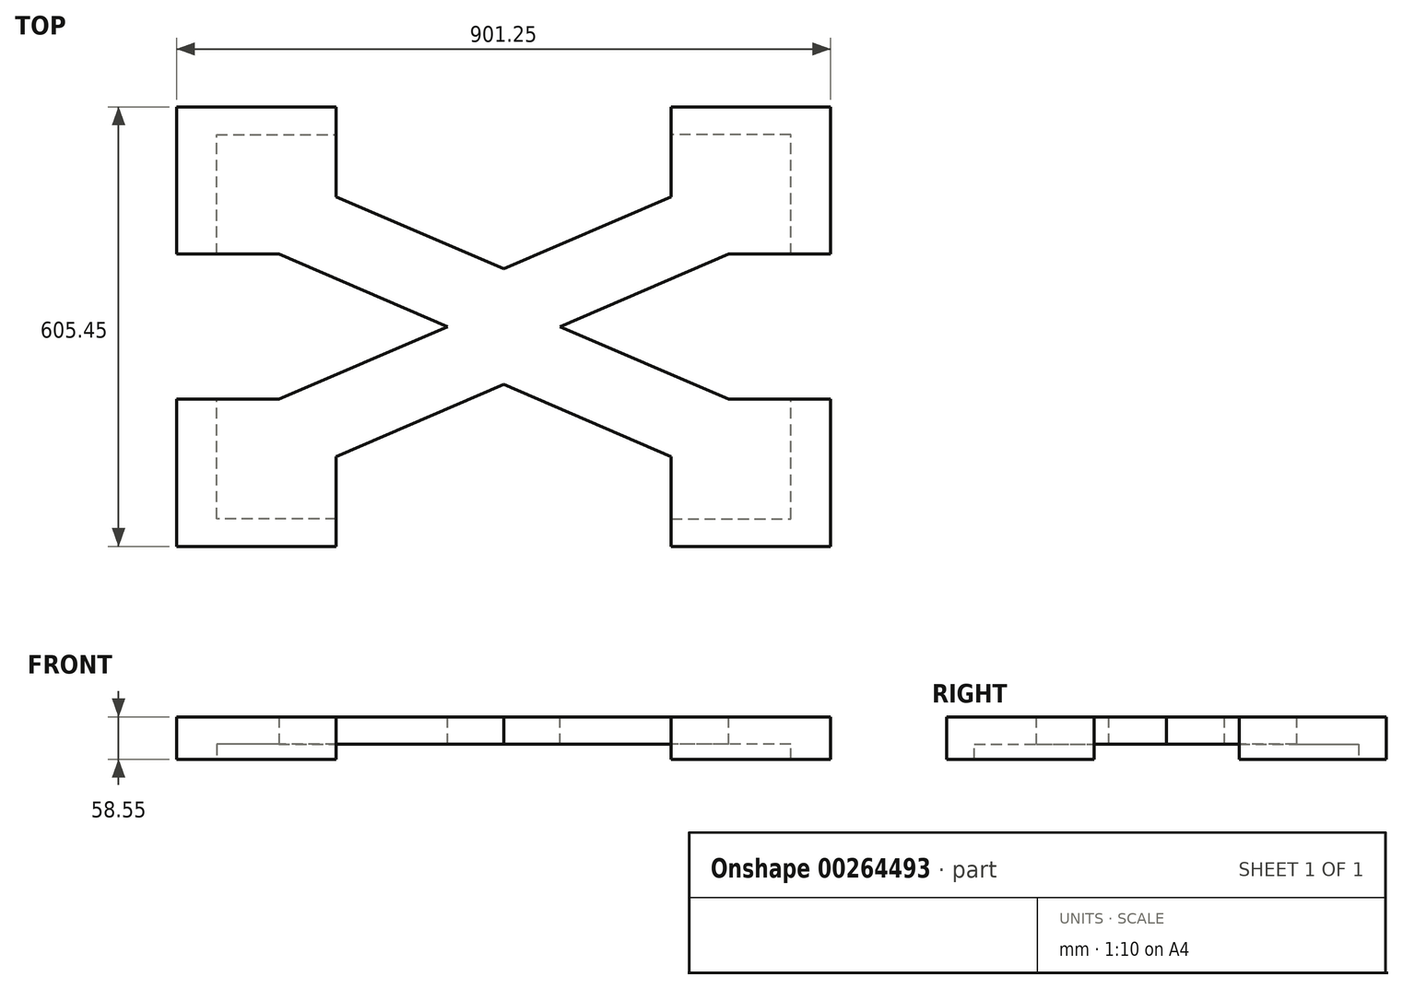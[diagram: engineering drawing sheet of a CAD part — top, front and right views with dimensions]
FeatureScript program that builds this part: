
annotation { "Feature Type Name" : "Feature", "Feature Type Description" : "" }
export const myFeature = defineFeature(function(context is Context, id is Id, definition is map)
    precondition{}
    {
        {
            var Q0;
            Q0=qCreatedBy(makeId("Top.planeOp"),FACE);
            var sketch = newSketch(context, id + "F0", { "sketchPlane" : qUnion([Q0])});
            skLineSegment(sketch, "E0", {"start": v(107.86, 53.86) * mm, "end": v(107.86, 107.86) * mm});
            skLineSegment(sketch, "E1", {"start": v(107.86, 107.86) * mm, "end": v(-107.86, 107.86) * mm});
            skLineSegment(sketch, "E2", {"start": v(-107.86, 107.86) * mm, "end": v(-107.86, -107.86) * mm});
            skLineSegment(sketch, "E3", {"start": v(-107.86, -107.86) * mm, "end": v(-53.86, -107.86) * mm});
            skLineSegment(sketch, "E4", {"start": v(-53.86, -107.86) * mm, "end": v(-53.86, 53.86) * mm});
            skLineSegment(sketch, "E5", {"start": v(-53.86, 53.86) * mm, "end": v(107.86, 53.86) * mm});
            skLineSegment(sketch, "E6", {"start": v(0, 107.86) * mm, "end": v(0, 0) * mm, "construction": true});
            skLineSegment(sketch, "E7", {"start": v(0, 0) * mm, "end": v(-107.86, 0) * mm, "construction": true});
            skSolve(sketch);
        }
        {
            var Q0;
            Q0=makeQuery(id+"F0.imprint","IMPRINT",FACE,{"disambiguationData":[TD([[makeQuery(id+"F0.imprint","IMPRINT",EDGE,{"derivedFrom":sQuery(id+"F0.wireOp",EDGE,"E0")}),1.0]])]});
            extrude(context, id + "F1", {"entities" : qUnion([Q0]), "depth" : 20.55 * mm});
        }
        {
            var Q0;
            Q0=makeQuery(id+"F1.opExtrude","CAP_FACE",FACE,{"disambiguationData":[OSD([sQuery(id+"F0.wireOp",EDGE,"E0"),sQuery(id+"F0.wireOp",EDGE,"E1"),sQuery(id+"F0.wireOp",EDGE,"E2"),sQuery(id+"F0.wireOp",EDGE,"E3"),sQuery(id+"F0.wireOp",EDGE,"E4"),sQuery(id+"F0.wireOp",EDGE,"E5")])],"isStart":false});
            var sketch = newSketch(context, id + "F2", { "sketchPlane" : qUnion([Q0])});
            skLineSegment(sketch, "E8.bottom", {"start": v(-107.86, 107.86) * mm, "end": v(107.86, 107.86) * mm});
            skLineSegment(sketch, "E8.top", {"start": v(-107.86, -107.86) * mm, "end": v(107.86, -107.86) * mm});
            skLineSegment(sketch, "E8.left", {"start": v(-107.86, 107.86) * mm, "end": v(-107.86, -107.86) * mm});
            skLineSegment(sketch, "E8.right", {"start": v(107.86, 107.86) * mm, "end": v(107.86, -107.86) * mm});
            skSolve(sketch);
        }
        {
            var Q0;
            Q0=qSketchRegion(id+"F2",true);
            extrude(context, id + "F3", {"entities" : qUnion([Q0]), "operationType" : NewBodyOperationType.ADD, "depth" : 38 * mm});
        }
        {
            var Q0;
            Q0=makeQuery(id+"F3.opExtrude","CAP_FACE",FACE,{"disambiguationData":[OSD([sQuery(id+"F2.wireOp",EDGE,"E8.bottom"),sQuery(id+"F2.wireOp",EDGE,"E8.top"),sQuery(id+"F2.wireOp",EDGE,"E8.left"),sQuery(id+"F2.wireOp",EDGE,"E8.right")])],"isStart":false});
            var sketch = newSketch(context, id + "F4", { "sketchPlane" : qUnion([Q0])});
            skLineSegment(sketch, "E9", {"start": v(-107.86, -107.86) * mm, "end": v(-110.86, -107.86) * mm});
            skLineSegment(sketch, "E10", {"start": v(-110.86, -107.86) * mm, "end": v(-110.86, 110.86) * mm});
            skLineSegment(sketch, "E11", {"start": v(-110.86, 110.86) * mm, "end": v(107.86, 110.86) * mm});
            skLineSegment(sketch, "E12", {"start": v(107.86, 110.86) * mm, "end": v(107.86, 107.86) * mm});
            skLineSegment(sketch, "E13", {"start": v(107.86, 107.86) * mm, "end": v(-107.86, 107.86) * mm});
            skLineSegment(sketch, "E14", {"start": v(-107.86, 107.86) * mm, "end": v(-107.86, -107.86) * mm});
            skSolve(sketch);
        }
        {
            var Q0;
            Q0=qSketchRegion(id+"F4",true);
            var Q1;
            Q1=makeQuery(id+"F1.opExtrude","CAP_FACE",FACE,{"disambiguationData":[OSD([sQuery(id+"F0.wireOp",EDGE,"E0"),sQuery(id+"F0.wireOp",EDGE,"E1"),sQuery(id+"F0.wireOp",EDGE,"E2"),sQuery(id+"F0.wireOp",EDGE,"E3"),sQuery(id+"F0.wireOp",EDGE,"E4"),sQuery(id+"F0.wireOp",EDGE,"E5")])],"isStart":true});
            extrude(context, id + "F5", {"entities" : qUnion([Q0]), "operationType" : NewBodyOperationType.ADD, "endBound" : BoundingType.UP_TO_SURFACE, "oppositeDirection" : true, "endBoundEntityFace" : qUnion([Q1]), "depth" : 25 * mm});
        }
        {
            var Q0;
            Q0=makeQuery(id+"F3.opExtrude","CAP_FACE",FACE,{"disambiguationData":[OSD([sQuery(id+"F2.wireOp",EDGE,"E8.bottom"),sQuery(id+"F2.wireOp",EDGE,"E8.top"),sQuery(id+"F2.wireOp",EDGE,"E8.left"),sQuery(id+"F2.wireOp",EDGE,"E8.right")])],"isStart":true});
            var sketch = newSketch(context, id + "F6", { "sketchPlane" : qUnion([Q0])});
            skLineSegment(sketch, "E15.bottom", {"start": v(31.86, 107.86) * mm, "end": v(107.86, 107.86) * mm});
            skLineSegment(sketch, "E15.top", {"start": v(31.86, 31.86) * mm, "end": v(107.86, 31.86) * mm});
            skLineSegment(sketch, "E15.left", {"start": v(31.86, 107.86) * mm, "end": v(31.86, 31.86) * mm});
            skLineSegment(sketch, "E15.right", {"start": v(107.86, 107.86) * mm, "end": v(107.86, 31.86) * mm});
            skSolve(sketch);
        }
        {
            var Q0;
            Q0=qSketchRegion(id+"F6",true);
            extrude(context, id + "F7", {"entities" : qUnion([Q0]), "operationType" : NewBodyOperationType.REMOVE, "endBound" : BoundingType.THROUGH_ALL, "oppositeDirection" : true, "depth" : 25 * mm});
        }
        {
            var Q0;
            Q0=makeQuery(id+"F5.boolean.opBoolean","MERGE",FACE,{"derivedFrom":[makeQuery(id+"F3.boolean.opBoolean","MERGE",FACE,{"derivedFrom":[makeQuery(id+"F1.opExtrude","SWEPT_FACE",FACE,{"disambiguationData":[OSD([sQuery(id+"F0.wireOp",EDGE,"E0")])]}),makeQuery(id+"F3.opExtrude","SWEPT_FACE",FACE,{"disambiguationData":[OSD([sQuery(id+"F2.wireOp",EDGE,"E8.right")])]})]}),makeQuery(id+"F5.opExtrude","SWEPT_FACE",FACE,{"disambiguationData":[OSD([sQuery(id+"F4.wireOp",EDGE,"E12")])]})]});
            var sketch = newSketch(context, id + "F8", { "sketchPlane" : qUnion([Q0])});
            skLineSegment(sketch, "E16", {"start": v(-31.86, 58.55) * mm, "end": v(-31.86, 20.55) * mm});
            skLineSegment(sketch, "E17", {"start": v(-31.86, 20.55) * mm, "end": v(53.86, 20.55) * mm});
            skLineSegment(sketch, "E18", {"start": v(53.86, 20.55) * mm, "end": v(53.86, 0) * mm});
            skLineSegment(sketch, "E19", {"start": v(53.86, 0) * mm, "end": v(110.86, 0) * mm});
            skLineSegment(sketch, "E20", {"start": v(110.86, 0) * mm, "end": v(110.86, 58.55) * mm});
            skLineSegment(sketch, "E21", {"start": v(110.86, 58.55) * mm, "end": v(-31.86, 58.55) * mm});
            skSolve(sketch);
        }
        {
            var Q0;
            Q0=qSketchRegion(id+"F8",true);
            extrude(context, id + "F9", {"entities" : qUnion([Q0]), "operationType" : NewBodyOperationType.ADD, "depth" : 3 * mm});
        }
        {
            var Q0;
            Q0=makeQuery(id+"F5.boolean.opBoolean","MERGE",FACE,{"derivedFrom":[makeQuery(id+"F3.boolean.opBoolean","MERGE",FACE,{"derivedFrom":[makeQuery(id+"F1.opExtrude","SWEPT_FACE",FACE,{"disambiguationData":[OSD([sQuery(id+"F0.wireOp",EDGE,"E3")])]}),makeQuery(id+"F3.opExtrude","SWEPT_FACE",FACE,{"disambiguationData":[OSD([sQuery(id+"F2.wireOp",EDGE,"E8.top")])]})]}),makeQuery(id+"F5.opExtrude","SWEPT_FACE",FACE,{"disambiguationData":[OSD([sQuery(id+"F4.wireOp",EDGE,"E9")])]})]});
            var sketch = newSketch(context, id + "F10", { "sketchPlane" : qUnion([Q0])});
            skLineSegment(sketch, "E22", {"start": v(-110.86, 58.55) * mm, "end": v(-110.86, 0) * mm});
            skLineSegment(sketch, "E23", {"start": v(-110.86, 0) * mm, "end": v(-53.86, 0) * mm});
            skLineSegment(sketch, "E24", {"start": v(-53.86, 0) * mm, "end": v(-53.86, 20.55) * mm});
            skLineSegment(sketch, "E25", {"start": v(-53.86, 20.55) * mm, "end": v(31.86, 20.55) * mm});
            skLineSegment(sketch, "E26", {"start": v(31.86, 20.55) * mm, "end": v(31.86, 58.55) * mm});
            skLineSegment(sketch, "E27", {"start": v(31.86, 58.55) * mm, "end": v(-110.86, 58.55) * mm});
            skSolve(sketch);
        }
        {
            var Q0;
            Q0=qSketchRegion(id+"F10",true);
            extrude(context, id + "F11", {"entities" : qUnion([Q0]), "operationType" : NewBodyOperationType.ADD, "depth" : 3 * mm});
        }
        {
            var Q0;
            {var subQ0=sQuery(id+"F0.wireOp",EDGE,"E5");var subQ1=sQuery(id+"F0.wireOp",EDGE,"E4");var subQ2=sQuery(id+"F0.wireOp",EDGE,"E3");var subQ3=sQuery(id+"F0.wireOp",EDGE,"E2");var subQ4=sQuery(id+"F0.wireOp",EDGE,"E1");var subQ5=sQuery(id+"F0.wireOp",EDGE,"E0");Q0=makeQuery(id+"F11.boolean.opBoolean","MERGE",FACE,{"derivedFrom":[makeQuery(id+"F9.boolean.opBoolean","MERGE",FACE,{"derivedFrom":[makeQuery(id+"F5.boolean.opBoolean","MERGE",FACE,{"derivedFrom":[makeQuery(id+"F1.opExtrude","CAP_FACE",FACE,{"disambiguationData":[OSD([subQ5,subQ4,subQ3,subQ2,subQ1,subQ0])],"isStart":true}),makeQuery(id+"F5.opExtrude","CAP_FACE",FACE,{"disambiguationData":[OSD([subQ5,subQ4,subQ3,subQ2,subQ1,subQ0])],"isStart":false})]}),makeQuery(id+"F9.opExtrude","SWEPT_FACE",FACE,{"disambiguationData":[OSD([sQuery(id+"F8.wireOp",EDGE,"E19")])]})]}),makeQuery(id+"F11.opExtrude","SWEPT_FACE",FACE,{"disambiguationData":[OSD([sQuery(id+"F10.wireOp",EDGE,"E23")])]})]});}
            var sketch = newSketch(context, id + "F12", { "sketchPlane" : qUnion([Q0])});
            skLineSegment(sketch, "E28.bottom", {"start": v(-110.86, -110.86) * mm, "end": v(110.86, -110.86) * mm});
            skLineSegment(sketch, "E28.top", {"start": v(-110.86, -91.86) * mm, "end": v(110.86, -91.86) * mm});
            skLineSegment(sketch, "E28.left", {"start": v(-110.86, -110.86) * mm, "end": v(-110.86, -91.86) * mm});
            skLineSegment(sketch, "E28.right", {"start": v(110.86, -110.86) * mm, "end": v(110.86, -91.86) * mm});
            skSolve(sketch);
        }
        {
            var Q0;
            Q0=qSketchRegion(id+"F12",true);
            extrude(context, id + "F13", {"entities" : qUnion([Q0]), "operationType" : NewBodyOperationType.REMOVE, "endBound" : BoundingType.THROUGH_ALL, "oppositeDirection" : true, "depth" : 25 * mm});
        }
        {
            var Q0;
            {var subQ0=sQuery(id+"F0.wireOp",EDGE,"E5");var subQ1=sQuery(id+"F0.wireOp",EDGE,"E4");var subQ2=sQuery(id+"F0.wireOp",EDGE,"E3");var subQ3=sQuery(id+"F0.wireOp",EDGE,"E2");var subQ4=sQuery(id+"F0.wireOp",EDGE,"E1");var subQ5=sQuery(id+"F0.wireOp",EDGE,"E0");Q0=makeQuery(id+"F11.boolean.opBoolean","MERGE",FACE,{"derivedFrom":[makeQuery(id+"F9.boolean.opBoolean","MERGE",FACE,{"derivedFrom":[makeQuery(id+"F5.boolean.opBoolean","MERGE",FACE,{"derivedFrom":[makeQuery(id+"F1.opExtrude","CAP_FACE",FACE,{"disambiguationData":[OSD([subQ5,subQ4,subQ3,subQ2,subQ1,subQ0])],"isStart":true}),makeQuery(id+"F5.opExtrude","CAP_FACE",FACE,{"disambiguationData":[OSD([subQ5,subQ4,subQ3,subQ2,subQ1,subQ0])],"isStart":false})]}),makeQuery(id+"F9.opExtrude","SWEPT_FACE",FACE,{"disambiguationData":[OSD([sQuery(id+"F8.wireOp",EDGE,"E19")])]})]}),makeQuery(id+"F11.opExtrude","SWEPT_FACE",FACE,{"disambiguationData":[OSD([sQuery(id+"F10.wireOp",EDGE,"E23")])]})]});}
            var sketch = newSketch(context, id + "F14", { "sketchPlane" : qUnion([Q0])});
            skLineSegment(sketch, "E29.bottom", {"start": v(-110.86, 110.86) * mm, "end": v(-108.86, 110.86) * mm});
            skLineSegment(sketch, "E29.top", {"start": v(-110.86, -91.86) * mm, "end": v(-108.86, -91.86) * mm});
            skLineSegment(sketch, "E29.left", {"start": v(-110.86, 110.86) * mm, "end": v(-110.86, -91.86) * mm});
            skLineSegment(sketch, "E29.right", {"start": v(-108.86, 110.86) * mm, "end": v(-108.86, -91.86) * mm});
            skSolve(sketch);
        }
        {
            var Q0;
            Q0=qSketchRegion(id+"F14",true);
            extrude(context, id + "F15", {"entities" : qUnion([Q0]), "operationType" : NewBodyOperationType.REMOVE, "endBound" : BoundingType.THROUGH_ALL, "oppositeDirection" : true, "depth" : 25 * mm});
        }
        {
            var Q0;
            Q0=makeQuery(id+"F11.boolean.opBoolean","MERGE",FACE,{"derivedFrom":[makeQuery(id+"F9.boolean.opBoolean","MERGE",FACE,{"derivedFrom":[makeQuery(id+"F5.boolean.opBoolean","MERGE",FACE,{"derivedFrom":[makeQuery(id+"F3.opExtrude","CAP_FACE",FACE,{"disambiguationData":[OSD([sQuery(id+"F2.wireOp",EDGE,"E8.bottom"),sQuery(id+"F2.wireOp",EDGE,"E8.top"),sQuery(id+"F2.wireOp",EDGE,"E8.left"),sQuery(id+"F2.wireOp",EDGE,"E8.right")])],"isStart":false}),makeQuery(id+"F5.opExtrude","CAP_FACE",FACE,{"disambiguationData":[OSD([sQuery(id+"F4.wireOp",EDGE,"E9"),sQuery(id+"F4.wireOp",EDGE,"E10"),sQuery(id+"F4.wireOp",EDGE,"E11"),sQuery(id+"F4.wireOp",EDGE,"E12"),sQuery(id+"F4.wireOp",EDGE,"E13"),sQuery(id+"F4.wireOp",EDGE,"E14")])],"isStart":true})]}),makeQuery(id+"F9.opExtrude","SWEPT_FACE",FACE,{"disambiguationData":[OSD([sQuery(id+"F8.wireOp",EDGE,"E21")])]})]}),makeQuery(id+"F11.opExtrude","SWEPT_FACE",FACE,{"disambiguationData":[OSD([sQuery(id+"F10.wireOp",EDGE,"E27")])]})]});
            var sketch = newSketch(context, id + "F16", { "sketchPlane" : qUnion([Q0])});
            skLineSegment(sketch, "E30.bottom", {"start": v(31.86, -31.86) * mm, "end": v(651.66, -31.86) * mm, "construction": true});
            skLineSegment(sketch, "E30.top", {"start": v(31.86, -389.86) * mm, "end": v(651.66, -389.86) * mm, "construction": true});
            skLineSegment(sketch, "E30.left", {"start": v(31.86, -31.86) * mm, "end": v(31.86, -389.86) * mm, "construction": true});
            skLineSegment(sketch, "E30.right", {"start": v(651.66, -31.86) * mm, "end": v(651.66, -389.86) * mm, "construction": true});
            skLineSegment(sketch, "E31", {"start": v(31.86, -31.86) * mm, "end": v(110.86, -31.86) * mm});
            skLineSegment(sketch, "E32", {"start": v(110.86, -31.86) * mm, "end": v(341.76, -131.22) * mm});
            skLineSegment(sketch, "E33", {"start": v(341.76, -131.22) * mm, "end": v(572.66, -31.86) * mm});
            skLineSegment(sketch, "E34", {"start": v(651.66, -110.86) * mm, "end": v(419.26, -210.86) * mm});
            skLineSegment(sketch, "E35", {"start": v(419.26, -210.86) * mm, "end": v(651.66, -310.86) * mm});
            skLineSegment(sketch, "E36", {"start": v(572.66, -389.86) * mm, "end": v(341.76, -290.5) * mm});
            skLineSegment(sketch, "E37", {"start": v(341.76, -290.5) * mm, "end": v(110.86, -389.86) * mm});
            skLineSegment(sketch, "E38", {"start": v(31.86, -310.86) * mm, "end": v(264.26, -210.86) * mm});
            skLineSegment(sketch, "E39", {"start": v(264.26, -210.86) * mm, "end": v(31.86, -110.86) * mm});
            skLineSegment(sketch, "E40", {"start": v(31.86, -110.86) * mm, "end": v(31.86, -31.86) * mm});
            skLineSegment(sketch, "E41", {"start": v(341.76, -389.86) * mm, "end": v(341.76, -31.86) * mm, "construction": true});
            skLineSegment(sketch, "E42", {"start": v(31.86, -210.86) * mm, "end": v(651.66, -210.86) * mm, "construction": true});
            skLineSegment(sketch, "E43", {"start": v(572.66, -31.86) * mm, "end": v(572.66, 91.86) * mm});
            skLineSegment(sketch, "E44", {"start": v(572.66, 91.86) * mm, "end": v(792.39, 91.86) * mm});
            skLineSegment(sketch, "E45", {"start": v(792.39, 91.86) * mm, "end": v(792.39, -110.86) * mm});
            skLineSegment(sketch, "E46", {"start": v(792.39, -110.86) * mm, "end": v(651.66, -110.86) * mm});
            skLineSegment(sketch, "E47", {"start": v(651.66, -310.86) * mm, "end": v(792.39, -310.86) * mm});
            skLineSegment(sketch, "E48", {"start": v(792.39, -310.86) * mm, "end": v(792.39, -513.59) * mm});
            skLineSegment(sketch, "E49", {"start": v(792.39, -513.59) * mm, "end": v(572.66, -513.59) * mm});
            skLineSegment(sketch, "E50", {"start": v(572.66, -513.59) * mm, "end": v(572.66, -389.86) * mm});
            skLineSegment(sketch, "E51", {"start": v(31.86, -310.86) * mm, "end": v(-108.86, -310.86) * mm});
            skLineSegment(sketch, "E52", {"start": v(-108.86, -310.86) * mm, "end": v(-108.86, -513.59) * mm});
            skLineSegment(sketch, "E53", {"start": v(-108.86, -513.59) * mm, "end": v(110.86, -513.59) * mm});
            skLineSegment(sketch, "E54", {"start": v(110.86, -513.59) * mm, "end": v(110.86, -389.86) * mm});
            skSolve(sketch);
        }
        {
            var Q0;
            Q0 = qSketchRegion(id + "F16", true);
            extrude(context, id + "F17", {"entities" : qUnion([Q0]), "operationType" : NewBodyOperationType.ADD, "oppositeDirection" : true, "depth" : 38 * mm});
        }
        {
            var Q0;
            Q0=makeQuery(id+"F17.boolean.opBoolean","MERGE",FACE,{"derivedFrom":[makeQuery(id+"F11.boolean.opBoolean","MERGE",FACE,{"derivedFrom":[makeQuery(id+"F9.boolean.opBoolean","MERGE",FACE,{"derivedFrom":[makeQuery(id+"F3.opExtrude","CAP_FACE",FACE,{"disambiguationData":[OSD([sQuery(id+"F2.wireOp",EDGE,"E8.bottom"),sQuery(id+"F2.wireOp",EDGE,"E8.top"),sQuery(id+"F2.wireOp",EDGE,"E8.left"),sQuery(id+"F2.wireOp",EDGE,"E8.right")])],"isStart":true}),makeQuery(id+"F9.opExtrude","SWEPT_FACE",FACE,{"disambiguationData":[OSD([sQuery(id+"F8.wireOp",EDGE,"E17")])]})]}),makeQuery(id+"F11.opExtrude","SWEPT_FACE",FACE,{"disambiguationData":[OSD([sQuery(id+"F10.wireOp",EDGE,"E25")])]})]}),makeQuery(id+"F17.opExtrude","CAP_FACE",FACE,{"disambiguationData":[OSD([sQuery(id+"F16.wireOp",EDGE,"E31"),sQuery(id+"F16.wireOp",EDGE,"E32"),sQuery(id+"F16.wireOp",EDGE,"E33"),sQuery(id+"F16.wireOp",EDGE,"E34"),sQuery(id+"F16.wireOp",EDGE,"E35"),sQuery(id+"F16.wireOp",EDGE,"E36"),sQuery(id+"F16.wireOp",EDGE,"E37"),sQuery(id+"F16.wireOp",EDGE,"E38"),sQuery(id+"F16.wireOp",EDGE,"E39"),sQuery(id+"F16.wireOp",EDGE,"E40"),sQuery(id+"F16.wireOp",EDGE,"E43"),sQuery(id+"F16.wireOp",EDGE,"E44"),sQuery(id+"F16.wireOp",EDGE,"E45"),sQuery(id+"F16.wireOp",EDGE,"E46"),sQuery(id+"F16.wireOp",EDGE,"E47"),sQuery(id+"F16.wireOp",EDGE,"E48"),sQuery(id+"F16.wireOp",EDGE,"E49"),sQuery(id+"F16.wireOp",EDGE,"E50"),sQuery(id+"F16.wireOp",EDGE,"E51"),sQuery(id+"F16.wireOp",EDGE,"E52"),sQuery(id+"F16.wireOp",EDGE,"E53"),sQuery(id+"F16.wireOp",EDGE,"E54")])],"isStart":false})]});
            var sketch = newSketch(context, id + "F18", { "sketchPlane" : qUnion([Q0])});
            skLineSegment(sketch, "E55", {"start": v(-53.86, 310.86) * mm, "end": v(-108.86, 310.86) * mm});
            skLineSegment(sketch, "E56", {"start": v(-108.86, 310.86) * mm, "end": v(-108.86, 513.59) * mm});
            skLineSegment(sketch, "E57", {"start": v(-108.86, 513.59) * mm, "end": v(110.86, 513.59) * mm});
            skLineSegment(sketch, "E58", {"start": v(110.86, 513.59) * mm, "end": v(110.86, 475.59) * mm});
            skLineSegment(sketch, "E59", {"start": v(110.86, 475.59) * mm, "end": v(-53.86, 475.59) * mm});
            skLineSegment(sketch, "E60", {"start": v(-53.86, 475.59) * mm, "end": v(-53.86, 310.86) * mm});
            skLineSegment(sketch, "E61", {"start": v(737.39, 310.86) * mm, "end": v(792.39, 310.86) * mm});
            skLineSegment(sketch, "E62", {"start": v(792.39, 310.86) * mm, "end": v(792.39, 513.59) * mm});
            skLineSegment(sketch, "E63", {"start": v(792.39, 513.59) * mm, "end": v(572.66, 513.59) * mm});
            skLineSegment(sketch, "E64", {"start": v(572.66, 513.59) * mm, "end": v(572.66, 475.59) * mm});
            skLineSegment(sketch, "E65", {"start": v(572.66, 475.59) * mm, "end": v(737.39, 475.59) * mm});
            skLineSegment(sketch, "E66", {"start": v(737.39, 475.59) * mm, "end": v(737.39, 310.86) * mm});
            skLineSegment(sketch, "E67", {"start": v(572.66, -53.86) * mm, "end": v(572.66, -91.86) * mm});
            skLineSegment(sketch, "E68", {"start": v(572.66, -91.86) * mm, "end": v(792.39, -91.86) * mm});
            skLineSegment(sketch, "E69", {"start": v(792.39, -91.86) * mm, "end": v(792.39, 110.86) * mm});
            skLineSegment(sketch, "E70", {"start": v(792.39, 110.86) * mm, "end": v(737.39, 110.86) * mm});
            skLineSegment(sketch, "E71", {"start": v(737.39, 110.86) * mm, "end": v(737.39, -53.86) * mm});
            skLineSegment(sketch, "E72", {"start": v(737.39, -53.86) * mm, "end": v(572.66, -53.86) * mm});
            skPoint(sketch, "E73", {"position": v(572.66, -30) * mm});
            skSolve(sketch);
        }
        {
            var Q0;
            Q0 = qSketchRegion(id + "F18", true);
            var Q1;
            {var subQ0=sQuery(id+"F0.wireOp",EDGE,"E5");var subQ1=sQuery(id+"F0.wireOp",EDGE,"E4");var subQ2=sQuery(id+"F0.wireOp",EDGE,"E3");var subQ3=sQuery(id+"F0.wireOp",EDGE,"E2");var subQ4=sQuery(id+"F0.wireOp",EDGE,"E1");var subQ5=sQuery(id+"F0.wireOp",EDGE,"E0");Q1=makeQuery(id+"F11.boolean.opBoolean","MERGE",FACE,{"derivedFrom":[makeQuery(id+"F9.boolean.opBoolean","MERGE",FACE,{"derivedFrom":[makeQuery(id+"F5.boolean.opBoolean","MERGE",FACE,{"derivedFrom":[makeQuery(id+"F1.opExtrude","CAP_FACE",FACE,{"disambiguationData":[OSD([subQ5,subQ4,subQ3,subQ2,subQ1,subQ0])],"isStart":true}),makeQuery(id+"F5.opExtrude","CAP_FACE",FACE,{"disambiguationData":[OSD([subQ5,subQ4,subQ3,subQ2,subQ1,subQ0])],"isStart":false})]}),makeQuery(id+"F9.opExtrude","SWEPT_FACE",FACE,{"disambiguationData":[OSD([sQuery(id+"F8.wireOp",EDGE,"E19")])]})]}),makeQuery(id+"F11.opExtrude","SWEPT_FACE",FACE,{"disambiguationData":[OSD([sQuery(id+"F10.wireOp",EDGE,"E23")])]})]});}
            extrude(context, id + "F19", {"entities" : qUnion([Q0]), "operationType" : NewBodyOperationType.ADD, "endBound" : BoundingType.UP_TO_SURFACE, "endBoundEntityFace" : qUnion([Q1]), "depth" : 25 * mm});
        }
    });
